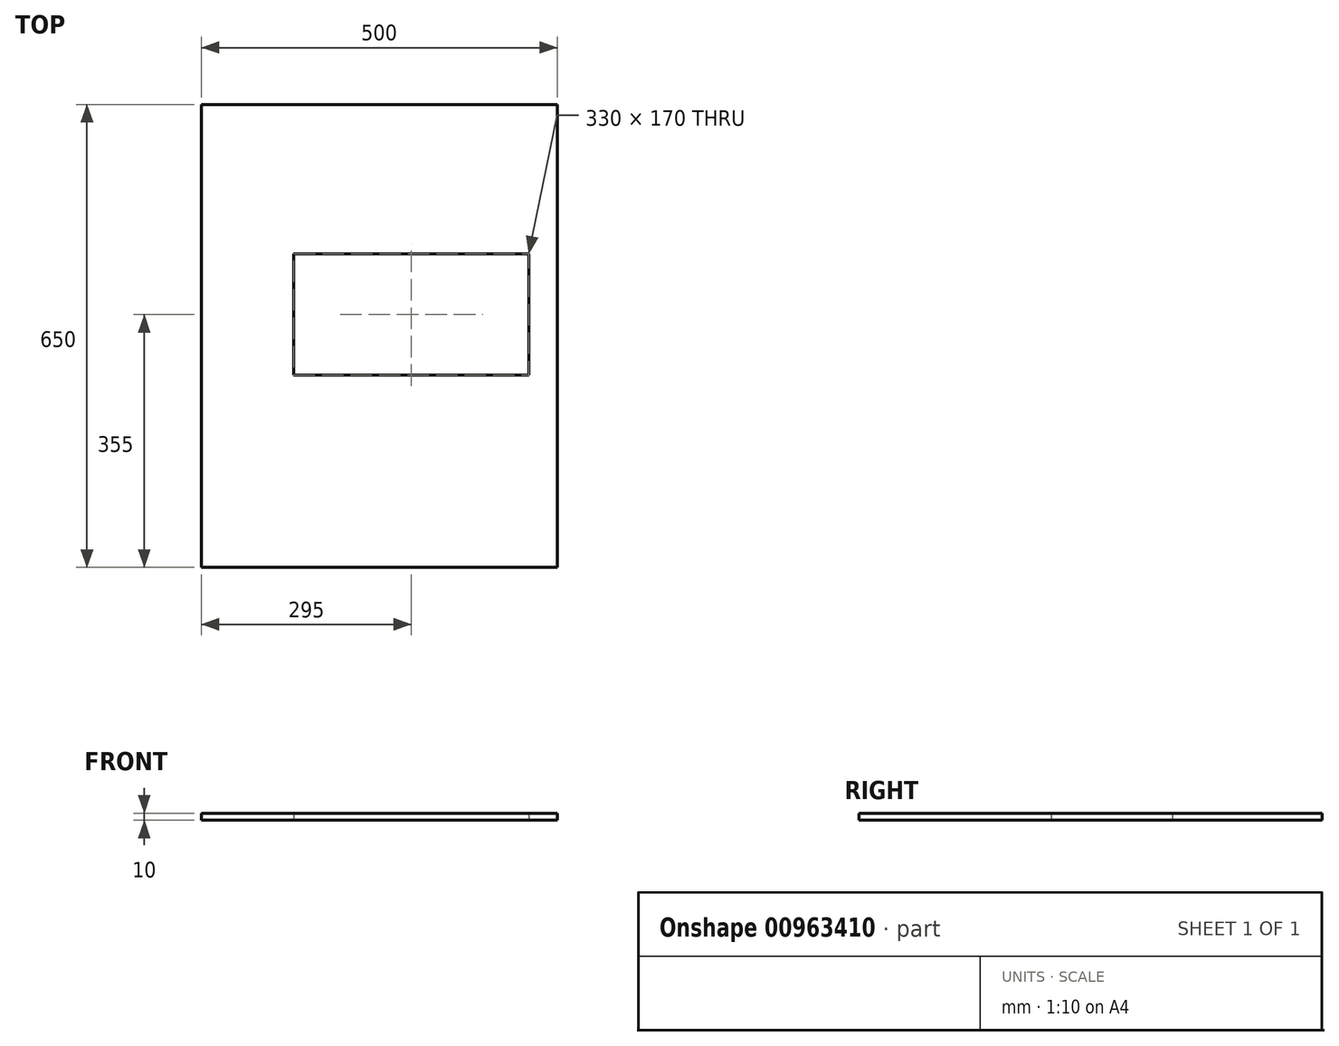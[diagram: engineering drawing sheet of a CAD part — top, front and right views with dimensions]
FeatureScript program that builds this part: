
annotation { "Feature Type Name" : "Feature", "Feature Type Description" : "" }
export const myFeature = defineFeature(function(context is Context, id is Id, definition is map)
    precondition{}
    {
        {
            var Q0;
            Q0=qCreatedBy(makeId("Top.planeOp"),FACE);
            var sketch = newSketch(context, id + "F0", { "sketchPlane" : qUnion([Q0])});
            skLineSegment(sketch, "E0.bottom", {"start": v(250, -325) * mm, "end": v(-250, -325) * mm});
            skLineSegment(sketch, "E0.top", {"start": v(250, 325) * mm, "end": v(-250, 325) * mm});
            skLineSegment(sketch, "E0.left", {"start": v(250, -325) * mm, "end": v(250, 325) * mm});
            skLineSegment(sketch, "E0.right", {"start": v(-250, -325) * mm, "end": v(-250, 325) * mm});
            skPoint(sketch, "E0.middle", {"position": v(0, 0) * mm});
            skLineSegment(sketch, "E1.bottom", {"start": v(-120, 115) * mm, "end": v(210, 115) * mm});
            skLineSegment(sketch, "E1.top", {"start": v(-120, -55) * mm, "end": v(210, -55) * mm});
            skLineSegment(sketch, "E1.left", {"start": v(-120, 115) * mm, "end": v(-120, -55) * mm});
            skLineSegment(sketch, "E1.right", {"start": v(210, 115) * mm, "end": v(210, -55) * mm});
            skSolve(sketch);
        }
        {
            var Q0;
            Q0=makeQuery(id+"F0.imprint","IMPRINT",FACE,{"disambiguationData":[TD([[makeQuery(id+"F0.imprint","IMPRINT",EDGE,{"derivedFrom":sQuery(id+"F0.wireOp",EDGE,"E0.bottom")}),-1.0]])]});
            extrude(context, id + "F1", {"entities" : qUnion([Q0]), "depth" : 10 * mm, "offsetDistance" : 25 * mm});
        }
    });
